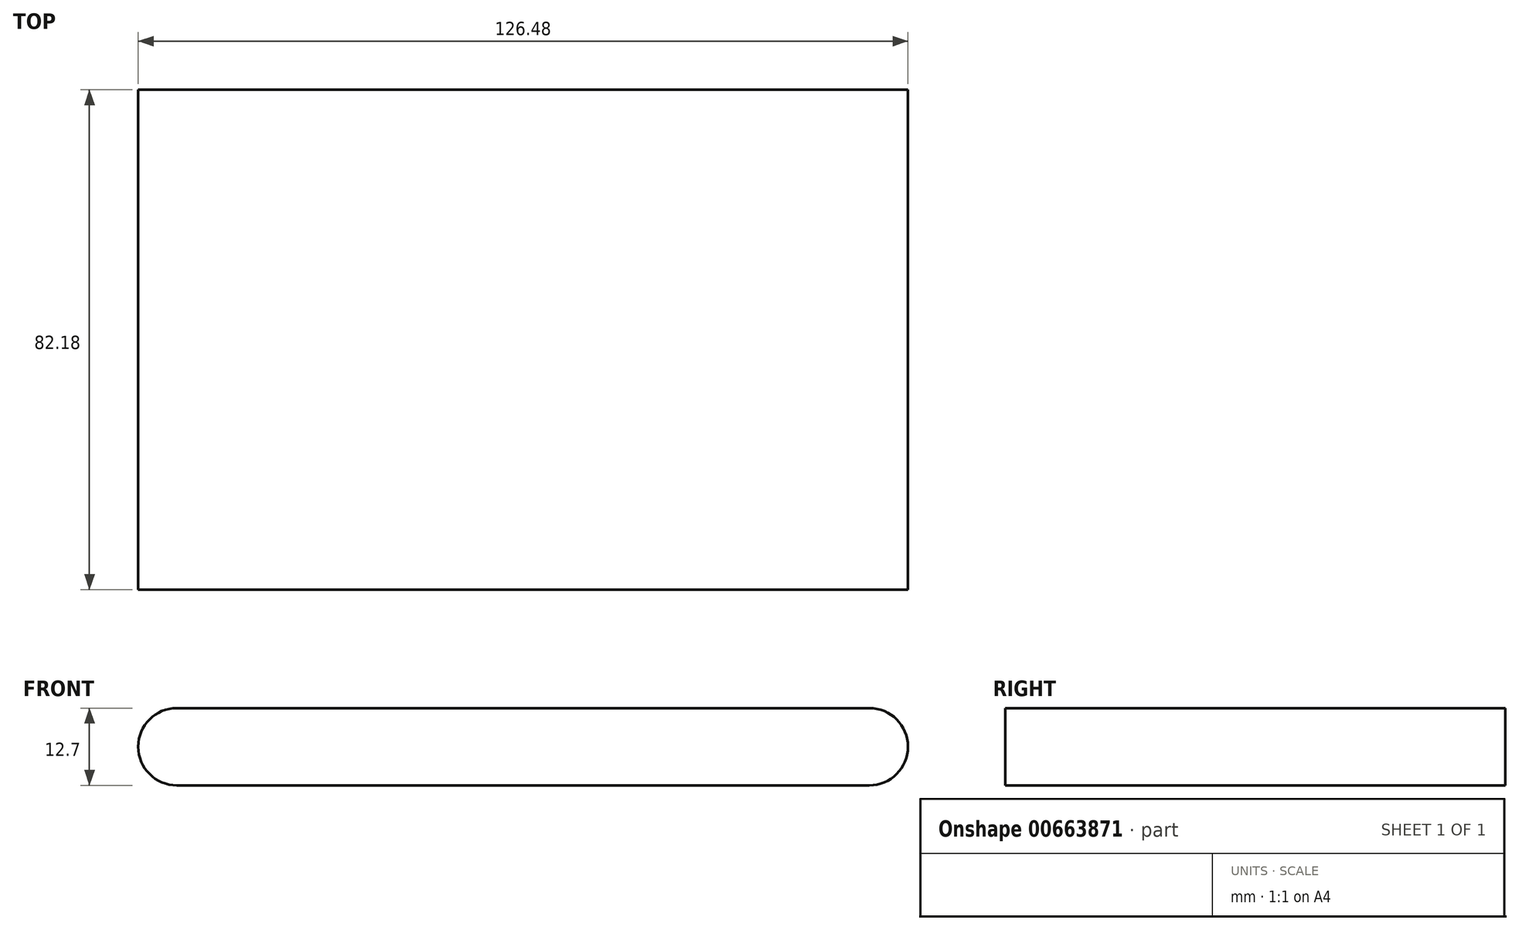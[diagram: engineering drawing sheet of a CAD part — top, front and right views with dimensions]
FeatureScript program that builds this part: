
annotation { "Feature Type Name" : "Feature", "Feature Type Description" : "" }
export const myFeature = defineFeature(function(context is Context, id is Id, definition is map)
    precondition{}
    {
        {
            var Q0;
            Q0=qCreatedBy(makeId("Front.planeOp"),FACE);
            var sketch = newSketch(context, id + "F0", { "sketchPlane" : qUnion([Q0])});
            skLineSegment(sketch, "E0", {"start": v(-50.95, 37.73) * mm, "end": v(62.83, 37.73) * mm, "construction": true});
            skArc(sketch, "E1.0.startCap", {"start": v(-50.95, 31.38) * mm, "mid": v(-57.3, 37.73) * mm, "end": v(-50.95, 44.08) * mm});
            skArc(sketch, "E1.0.endCap", {"start": v(62.83, 44.08) * mm, "mid": v(69.18, 37.73) * mm, "end": v(62.83, 31.38) * mm});
            skLineSegment(sketch, "E1.0.left", {"start": v(-50.95, 44.08) * mm, "end": v(62.83, 44.08) * mm});
            skLineSegment(sketch, "E1.0.right", {"start": v(-50.95, 31.38) * mm, "end": v(62.83, 31.38) * mm});
            skSolve(sketch);
        }
        {
            var Q0;
            Q0=makeQuery(id+"F0.imprint","IMPRINT",FACE,{"disambiguationData":[TD([[makeQuery(id+"F0.imprint","IMPRINT",EDGE,{"derivedFrom":sQuery(id+"F0.wireOp",EDGE,"E1.0.startCap")}),-1.0]])]});
            var Q1;
            Q1 = qBodyType(qCreatedBy(id + "F0" ,EDGE), BodyType.WIRE);
            var Q2;
            Q2=sQuery(id+"F0.wireOp",EDGE,"E1.0.endCap");
            var Q3;
            Q3=sQuery(id+"F0.wireOp",EDGE,"E1.0.startCap");
            var Q4;
            Q4=sQuery(id+"F0.wireOp",EDGE,"E1.0.left");
            extrude(context, id + "F1", {"entities" : qUnion([Q0]), "bodyType" : ToolBodyType.SURFACE, "surfaceEntities" : qUnion([Q1, Q2, Q3, Q4]), "depth" : 82.18 * mm, "offsetDistance" : 25.4 * mm});
        }
    });
